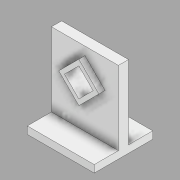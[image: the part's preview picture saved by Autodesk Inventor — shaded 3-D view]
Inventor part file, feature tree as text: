
AUTODESK INVENTOR PART (.ipt)
format: ipt  version: 2020 (Build 240168000, 168)  size: 131,072 bytes
history: native  units: in
note: dims shown in document units (in); Inventor stores cm internally (conversion verified against a paired STEP export)
features: extrude x3, sketch x1, projected_geometry x1
ambient origin geometry x8: Origin, YZ Plane, XZ Plane, XY Plane, X Axis, Y Axis, Z Axis, Center Point
bodies: Solid1 (feature_tree)
feature tree (5):
  extrude  "Extrusion2"  TaperAngle=0.0deg  [1 undecoded]
  extrude  "Extrusion3"  Depth=0.2in
  extrude  "Extrusion4"  Depth=0.2in
  sketch  "Sketch2"  dims[d0=1.0in d1=1.0in d5=0.0in d6=0.2in d7=0.2in d13=0.8in d14=0.0in d15=3.3in d16=4.0in d17=0.5in d18=0.0in d19=0.5in d20=0.0in]
  projected_geometry  "Projected Loop1"
note: 1 required parameter value undecoded (feature->parameter linkage not recoverable at this tier; creation-order binding heuristic only, values carry confidence <= 0.55)
